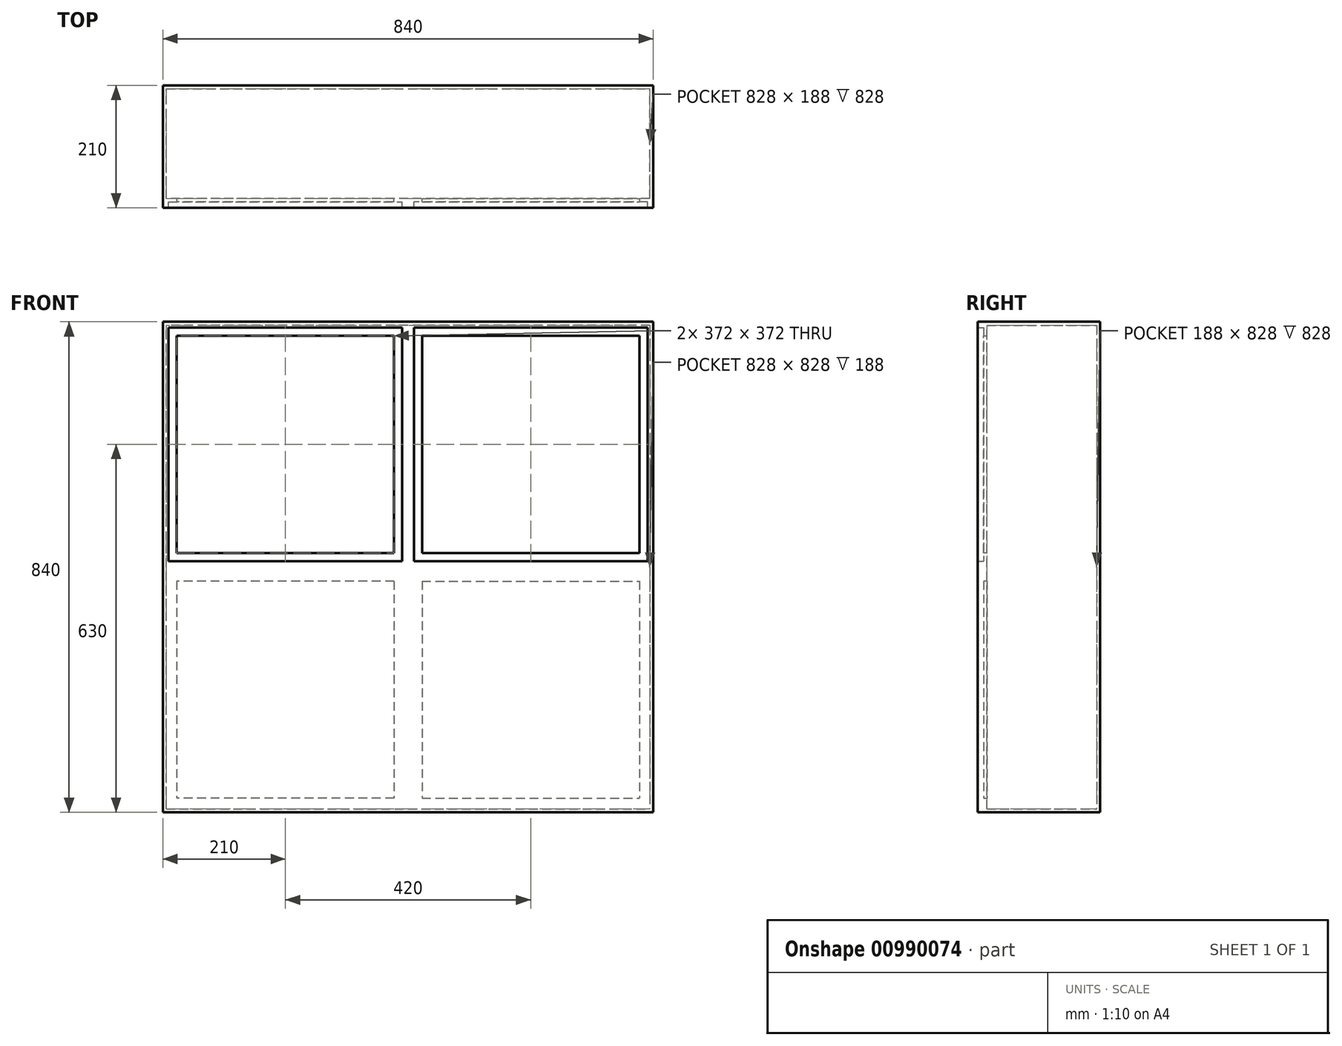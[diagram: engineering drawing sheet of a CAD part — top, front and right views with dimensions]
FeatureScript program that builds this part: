
annotation { "Feature Type Name" : "Feature", "Feature Type Description" : "" }
export const myFeature = defineFeature(function(context is Context, id is Id, definition is map)
    precondition{}
    {
        {
            var Q0;
            Q0=qCreatedBy(makeId("Front.planeOp"),FACE);
            var sketch = newSketch(context, id + "F0", { "sketchPlane" : qUnion([Q0])});
            skLineSegment(sketch, "E0.bottom", {"start": v(-210, 210) * mm, "end": v(210, 210) * mm});
            skLineSegment(sketch, "E0.top", {"start": v(-210, -210) * mm, "end": v(210, -210) * mm});
            skLineSegment(sketch, "E0.left", {"start": v(-210, 210) * mm, "end": v(-210, -210) * mm});
            skLineSegment(sketch, "E0.right", {"start": v(210, 210) * mm, "end": v(210, -210) * mm});
            skPoint(sketch, "E0.middle", {"position": v(0, 0) * mm});
            skSolve(sketch);
        }
        {
            var Q0;
            Q0=qSketchRegion(id+"F0",true);
            extrude(context, id + "F1", {"entities" : qUnion([Q0]), "endBound" : BoundingType.SYMMETRIC, "depth" : 210 * mm, "offsetDistance" : 25.4 * mm});
        }
        {
            var Q0;
            Q0=makeQuery(id+"F1.opExtrude","CAP_FACE",FACE,{"disambiguationData":[OSD([sQuery(id+"F0.wireOp",EDGE,"E0.bottom"),sQuery(id+"F0.wireOp",EDGE,"E0.top"),sQuery(id+"F0.wireOp",EDGE,"E0.left"),sQuery(id+"F0.wireOp",EDGE,"E0.right")])],"isStart":false});
            shell(context, id + "F2", {"entities" : qUnion([Q0]), "thickness" : 6 * mm});
        }
        {
            var Q0;
            Q0=makeQuery(id+"F2.opShell","OFFSET_FACE",FACE,{"disambiguationData":[OSD([sQuery(id+"F0.wireOp",EDGE,"E0.left")])]});
            var sketch = newSketch(context, id + "F3", { "sketchPlane" : qUnion([Q0])});
            skLineSegment(sketch, "E1.top", {"start": v(-2, -194) * mm, "end": v(2, -194) * mm});
            skPoint(sketch, "E1.middle", {"position": v(0, 0) * mm});
            skLineSegment(sketch, "E2.bottom", {"start": v(-89, -204) * mm, "end": v(-95, -204) * mm});
            skLineSegment(sketch, "E2.top", {"start": v(-89, 204) * mm, "end": v(-95, 204) * mm});
            skLineSegment(sketch, "E2.left", {"start": v(-89, -204) * mm, "end": v(-89, 204) * mm});
            skLineSegment(sketch, "E2.right", {"start": v(-95, -204) * mm, "end": v(-95, 204) * mm});
            skPoint(sketch, "E2.middle", {"position": v(-92, 0) * mm});
            skSolve(sketch);
        }
        {
            var Q0;
            Q0=qSketchRegion(id+"F3",true);
            extrude(context, id + "F4", {"entities" : qUnion([Q0]), "operationType" : NewBodyOperationType.ADD, "depth" : 18 * mm, "offsetDistance" : 25.4 * mm});
        }
        {
            var Q0;
            Q0=makeQuery(id+"F2.opShell","OFFSET_FACE",FACE,{"disambiguationData":[OSD([sQuery(id+"F0.wireOp",EDGE,"E0.right")])]});
            var sketch = newSketch(context, id + "F5", { "sketchPlane" : qUnion([Q0])});
            skLineSegment(sketch, "E3.bottom", {"start": v(95, -204) * mm, "end": v(89, -204) * mm});
            skLineSegment(sketch, "E3.top", {"start": v(95, 204) * mm, "end": v(89, 204) * mm});
            skLineSegment(sketch, "E3.left", {"start": v(89, -204) * mm, "end": v(89, 204) * mm});
            skLineSegment(sketch, "E3.right", {"start": v(95, -204) * mm, "end": v(95, 204) * mm});
            skPoint(sketch, "E3.middle", {"position": v(92, 0) * mm});
            skSolve(sketch);
        }
        {
            var Q0;
            Q0=qSketchRegion(id+"F5",true);
            extrude(context, id + "F6", {"entities" : qUnion([Q0]), "operationType" : NewBodyOperationType.ADD, "depth" : 18 * mm, "offsetDistance" : 25.4 * mm});
        }
        {
            var Q0;
            Q0=makeQuery(id+"F4.opExtrude","CAP_FACE",FACE,{"disambiguationData":[OSD([sQuery(id+"F3.wireOp",EDGE,"E2.bottom"),sQuery(id+"F3.wireOp",EDGE,"E2.top"),sQuery(id+"F3.wireOp",EDGE,"E2.left"),sQuery(id+"F3.wireOp",EDGE,"E2.right")])],"isStart":false});
            var sketch = newSketch(context, id + "F7", { "sketchPlane" : qUnion([Q0])});
            skLineSegment(sketch, "E4.bottom", {"start": v(-95, 204) * mm, "end": v(-89, 204) * mm});
            skLineSegment(sketch, "E4.top", {"start": v(-95, 186) * mm, "end": v(-89, 186) * mm});
            skLineSegment(sketch, "E4.left", {"start": v(-95, 204) * mm, "end": v(-95, 186) * mm});
            skLineSegment(sketch, "E4.right", {"start": v(-89, 204) * mm, "end": v(-89, 186) * mm});
            skSolve(sketch);
        }
        {
            var Q0;
            Q0=qSketchRegion(id+"F7",true);
            var Q1;
            Q1=makeQuery(id+"F6.opExtrude","CAP_FACE",FACE,{"disambiguationData":[OSD([sQuery(id+"F5.wireOp",EDGE,"E3.bottom"),sQuery(id+"F5.wireOp",EDGE,"E3.top"),sQuery(id+"F5.wireOp",EDGE,"E3.left"),sQuery(id+"F5.wireOp",EDGE,"E3.right")])],"isStart":false});
            extrude(context, id + "F8", {"entities" : qUnion([Q0]), "operationType" : NewBodyOperationType.ADD, "endBound" : BoundingType.UP_TO_SURFACE, "depth" : 12.2 * mm, "endBoundEntityFace" : qUnion([Q1]), "offsetDistance" : 25.4 * mm});
        }
        {
            var Q0;
            Q0=makeQuery(id+"F4.opExtrude","CAP_FACE",FACE,{"disambiguationData":[OSD([sQuery(id+"F3.wireOp",EDGE,"E2.bottom"),sQuery(id+"F3.wireOp",EDGE,"E2.top"),sQuery(id+"F3.wireOp",EDGE,"E2.left"),sQuery(id+"F3.wireOp",EDGE,"E2.right")])],"isStart":false});
            var sketch = newSketch(context, id + "F9", { "sketchPlane" : qUnion([Q0])});
            skLineSegment(sketch, "E5.bottom", {"start": v(-89, -204) * mm, "end": v(-95, -204) * mm});
            skLineSegment(sketch, "E5.top", {"start": v(-89, -186) * mm, "end": v(-95, -186) * mm});
            skLineSegment(sketch, "E5.left", {"start": v(-89, -204) * mm, "end": v(-89, -186) * mm});
            skLineSegment(sketch, "E5.right", {"start": v(-95, -204) * mm, "end": v(-95, -186) * mm});
            skSolve(sketch);
        }
        {
            var Q0;
            Q0=qSketchRegion(id+"F9",true);
            var Q1;
            Q1=makeQuery(id+"F6.opExtrude","CAP_FACE",FACE,{"disambiguationData":[OSD([sQuery(id+"F5.wireOp",EDGE,"E3.bottom"),sQuery(id+"F5.wireOp",EDGE,"E3.top"),sQuery(id+"F5.wireOp",EDGE,"E3.left"),sQuery(id+"F5.wireOp",EDGE,"E3.right")])],"isStart":false});
            extrude(context, id + "F10", {"entities" : qUnion([Q0]), "operationType" : NewBodyOperationType.ADD, "endBound" : BoundingType.UP_TO_SURFACE, "depth" : 25.4 * mm, "endBoundEntityFace" : qUnion([Q1]), "offsetDistance" : 25.4 * mm});
        }
        {
            var Q0;
            Q0=makeQuery(id+"F10.boolean.opBoolean","MERGE",FACE,{"derivedFrom":[makeQuery(id+"F8.boolean.opBoolean","MERGE",FACE,{"derivedFrom":[makeQuery(id+"F4.opExtrude","SWEPT_FACE",FACE,{"disambiguationData":[OSD([sQuery(id+"F3.wireOp",EDGE,"E2.right")])]}),makeQuery(id+"F6.opExtrude","SWEPT_FACE",FACE,{"disambiguationData":[OSD([sQuery(id+"F5.wireOp",EDGE,"E3.right")])]}),makeQuery(id+"F8.opExtrude","SWEPT_FACE",FACE,{"disambiguationData":[OSD([sQuery(id+"F7.wireOp",EDGE,"E4.left")])]})]}),makeQuery(id+"F10.opExtrude","SWEPT_FACE",FACE,{"disambiguationData":[OSD([sQuery(id+"F9.wireOp",EDGE,"E5.right")])]})]});
            var sketch = newSketch(context, id + "F11", { "sketchPlane" : qUnion([Q0])});
            skLineSegment(sketch, "E6.bottom", {"start": v(-204, 204) * mm, "end": v(204, 204) * mm});
            skLineSegment(sketch, "E6.top", {"start": v(-204, -204) * mm, "end": v(204, -204) * mm});
            skLineSegment(sketch, "E6.left", {"start": v(-204, 204) * mm, "end": v(-204, -204) * mm});
            skLineSegment(sketch, "E6.right", {"start": v(204, 204) * mm, "end": v(204, -204) * mm});
            skPoint(sketch, "E6.middle", {"position": v(0, 0) * mm});
            skLineSegment(sketch, "E7.bottom", {"start": v(-200, 200) * mm, "end": v(200, 200) * mm});
            skLineSegment(sketch, "E7.top", {"start": v(-200, -200) * mm, "end": v(200, -200) * mm});
            skLineSegment(sketch, "E7.left", {"start": v(-200, 200) * mm, "end": v(-200, -200) * mm});
            skLineSegment(sketch, "E7.right", {"start": v(200, 200) * mm, "end": v(200, -200) * mm});
            skSolve(sketch);
        }
        {
            var Q0;
            Q0=qSketchRegion(id+"F11",true);
            extrude(context, id + "F12", {"entities" : qUnion([Q0]), "operationType" : NewBodyOperationType.ADD, "depth" : 10 * mm, "offsetDistance" : 25.4 * mm});
        }
        {
            var Q0;
            Q0=makeQuery(id+"F1.opExtrude","SWEPT_BODY",BODY,{"disambiguationData":[OSD([sQuery(id+"F0.wireOp",EDGE,"E0.bottom"),sQuery(id+"F0.wireOp",EDGE,"E0.top"),sQuery(id+"F0.wireOp",EDGE,"E0.left"),sQuery(id+"F0.wireOp",EDGE,"E0.right")])]});
            var Q1;
            Q1=makeQuery(id+"F1.opExtrude","SWEPT_FACE",FACE,{"disambiguationData":[OSD([sQuery(id+"F0.wireOp",EDGE,"E0.top")])]});
            mirror(context, id + "F13", {"operationType" : NewBodyOperationType.ADD, "entities" : qUnion([Q0]), "mirrorPlane" : qUnion([Q1])});
        }
        {
            var Q0;
            Q0=makeQuery(id+"F13.opPattern","COPY",FACE,{"derivedFrom":makeQuery(id+"F10.boolean.opBoolean","MERGE",FACE,{"derivedFrom":[makeQuery(id+"F8.boolean.opBoolean","MERGE",FACE,{"derivedFrom":[makeQuery(id+"F4.opExtrude","SWEPT_FACE",FACE,{"disambiguationData":[OSD([sQuery(id+"F3.wireOp",EDGE,"E2.right")])]}),makeQuery(id+"F6.opExtrude","SWEPT_FACE",FACE,{"disambiguationData":[OSD([sQuery(id+"F5.wireOp",EDGE,"E3.right")])]}),makeQuery(id+"F8.opExtrude","SWEPT_FACE",FACE,{"disambiguationData":[OSD([sQuery(id+"F7.wireOp",EDGE,"E4.left")])]})]}),makeQuery(id+"F10.opExtrude","SWEPT_FACE",FACE,{"disambiguationData":[OSD([sQuery(id+"F9.wireOp",EDGE,"E5.right")])]})]}),"instanceName":"1"});
            var sketch = newSketch(context, id + "F14", { "sketchPlane" : qUnion([Q0])});
            skLineSegment(sketch, "E8.bottom", {"start": v(-200, -220) * mm, "end": v(200, -220) * mm});
            skLineSegment(sketch, "E8.top", {"start": v(-200, -620) * mm, "end": v(200, -620) * mm});
            skLineSegment(sketch, "E8.left", {"start": v(-200, -220) * mm, "end": v(-200, -620) * mm});
            skLineSegment(sketch, "E8.right", {"start": v(200, -220) * mm, "end": v(200, -620) * mm});
            skSolve(sketch);
        }
        {
            var Q0;
            Q0=qSketchRegion(id+"F14",true);
            extrude(context, id + "F15", {"entities" : qUnion([Q0]), "operationType" : NewBodyOperationType.ADD, "depth" : 10 * mm, "offsetDistance" : 25.4 * mm});
        }
        {
            var Q0;
            {var subQ2=sQuery(id+"F0.wireOp",EDGE,"E0.top");Q0=makeQuery(id+"F10.boolean.opBoolean","SPLIT",FACE,{"disambiguationData":[TD([makeQuery(id+"F4.opExtrude","SWEPT_FACE",FACE,{"disambiguationData":[OSD([sQuery(id+"F3.wireOp",EDGE,"E2.left")])]})])],"derivedFrom":makeQuery(id+"F2.opShell","OFFSET_FACE",FACE,{"disambiguationData":[OSD([subQ2])]})});}
            extrude(context, id + "F16", {"entities" : qUnion([Q0]), "operationType" : NewBodyOperationType.REMOVE, "oppositeDirection" : true, "depth" : 25.4 * mm, "offsetDistance" : 25.4 * mm});
        }
        {
            var Q0;
            Q0=makeQuery(id+"F1.opExtrude","SWEPT_BODY",BODY,{"disambiguationData":[OSD([sQuery(id+"F0.wireOp",EDGE,"E0.bottom"),sQuery(id+"F0.wireOp",EDGE,"E0.top"),sQuery(id+"F0.wireOp",EDGE,"E0.left"),sQuery(id+"F0.wireOp",EDGE,"E0.right")])]});
            var Q1;
            {var subQ0=makeQuery(id+"F1.opExtrude","SWEPT_FACE",FACE,{"disambiguationData":[OSD([sQuery(id+"F0.wireOp",EDGE,"E0.right")])]});Q1=makeQuery(id+"F13.boolean.opBoolean","MERGE",FACE,{"derivedFrom":[subQ0,makeQuery(id+"F13.opPattern","COPY",FACE,{"derivedFrom":subQ0,"instanceName":"1"})]});}
            mirror(context, id + "F17", {"operationType" : NewBodyOperationType.ADD, "entities" : qUnion([Q0]), "mirrorPlane" : qUnion([Q1])});
        }
        {
            var Q0;
            {var subQ0=sQuery(id+"F0.wireOp",EDGE,"E0.right");var subQ1=sQuery(id+"F0.wireOp",EDGE,"E0.top");var subQ3=makeQuery(id+"F6.boolean.opBoolean","SPLIT",FACE,{"disambiguationData":[TD([makeQuery(id+"F6.opExtrude","SWEPT_FACE",FACE,{"disambiguationData":[OSD([sQuery(id+"F5.wireOp",EDGE,"E3.left")])]})])],"derivedFrom":makeQuery(id+"F2.opShell","OFFSET_FACE",FACE,{"disambiguationData":[OSD([subQ0])]})});Q0=makeQuery(id+"F17.opPattern","COPY",FACE,{"derivedFrom":makeQuery(id+"F16.boolean.opBoolean","MERGE",FACE,{"derivedFrom":[subQ3,makeQuery(id+"F13.opPattern","COPY",FACE,{"derivedFrom":subQ3,"instanceName":"1"})],"fromTools":[makeQuery(id+"F16.opExtrude","SWEPT_FACE",FACE,{"disambiguationData":[OSD([subQ1,subQ0])]})]}),"instanceName":"1"});}
            extrude(context, id + "F18", {"entities" : qUnion([Q0]), "operationType" : NewBodyOperationType.REMOVE, "oppositeDirection" : true, "depth" : 25.4 * mm, "offsetDistance" : 25.4 * mm});
        }
    });
